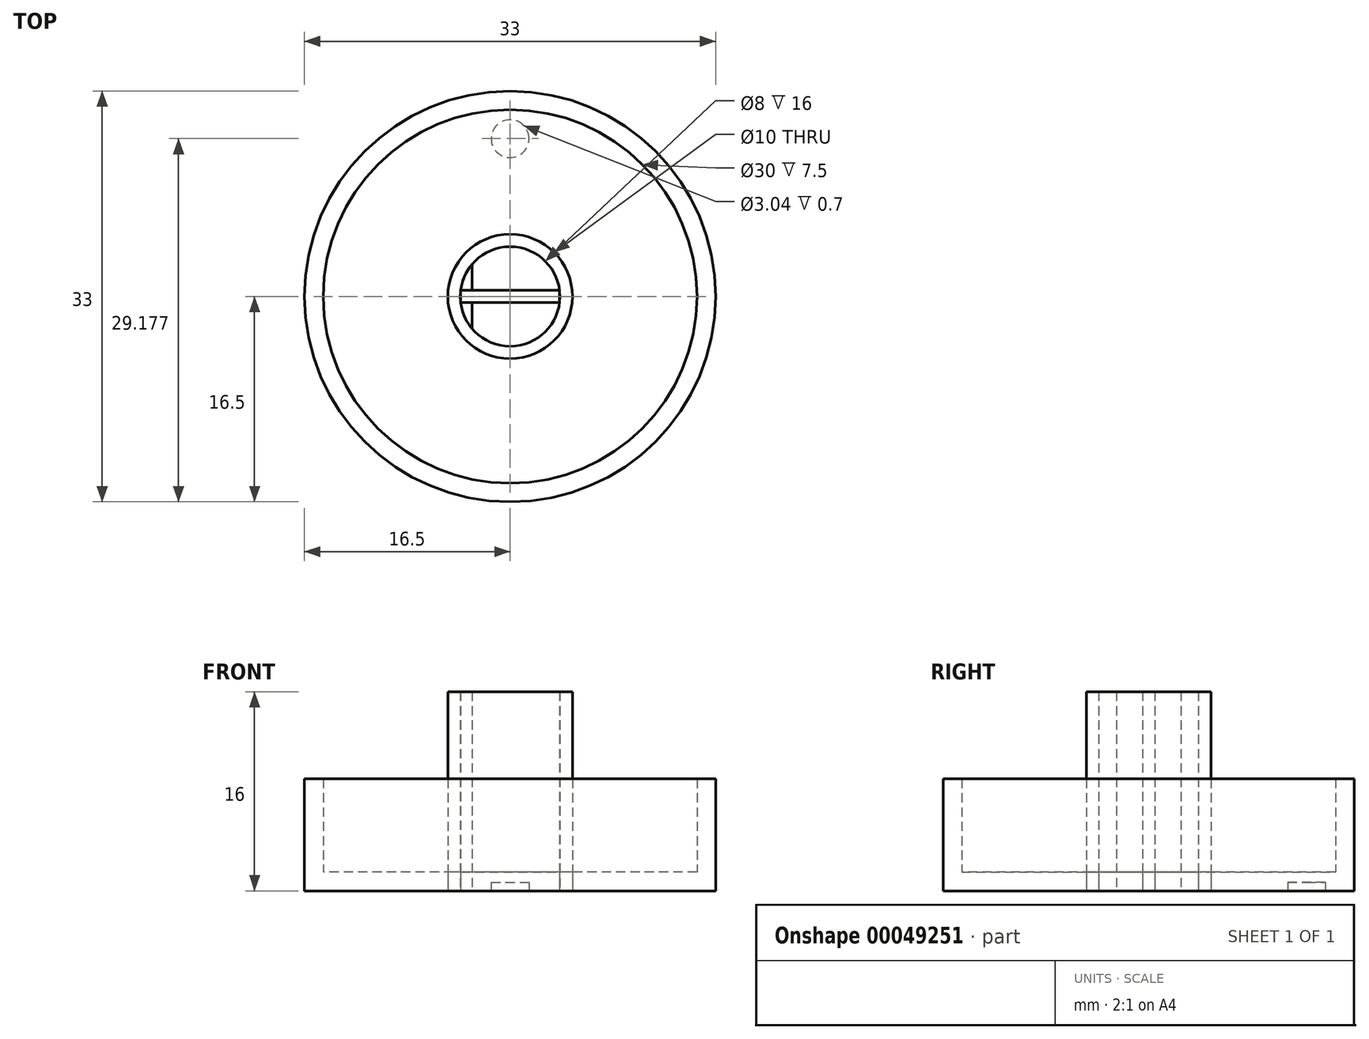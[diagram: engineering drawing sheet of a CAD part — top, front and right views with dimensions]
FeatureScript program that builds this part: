
annotation { "Feature Type Name" : "Feature", "Feature Type Description" : "" }
export const myFeature = defineFeature(function(context is Context, id is Id, definition is map)
    precondition{}
    {
        {
            var Q0;
            Q0=qCreatedBy(makeId("Top.planeOp"),FACE);
            var sketch = newSketch(context, id + "F0", { "sketchPlane" : qUnion([Q0])});
            skCircle(sketch, "E0", {"center": v(0, 0) * mm, "radius": 16.5 * mm});
            skCircle(sketch, "E1", {"center": v(0, 0) * mm, "radius": 15 * mm});
            skCircle(sketch, "E2", {"center": v(0, 0) * mm, "radius": 5 * mm});
            skCircle(sketch, "E3", {"center": v(0, 0) * mm, "radius": 4 * mm});
            skLineSegment(sketch, "E4.rect.bottom", {"start": v(-3.97, 0.5) * mm, "end": v(3.97, 0.5) * mm});
            skLineSegment(sketch, "E4.rect.top", {"start": v(-3.97, -0.5) * mm, "end": v(3.97, -0.5) * mm});
            skLineSegment(sketch, "E4.rect.left", {"start": v(-3.97, 0.5) * mm, "end": v(-3.97, -0.5) * mm});
            skLineSegment(sketch, "E4.rect.right", {"start": v(3.97, 0.5) * mm, "end": v(3.97, -0.5) * mm});
            skLineSegment(sketch, "E5", {"start": v(-3.05, 2.59) * mm, "end": v(-3.05, -2.59) * mm});
            skSolve(sketch);
        }
        {
            var Q0;
            Q0=makeQuery(id+"F0.imprint","IMPRINT",FACE,{"disambiguationData":[TD([[makeQuery(id+"F0.imprint","IMPRINT",EDGE,{"derivedFrom":sQuery(id+"F0.wireOp",EDGE,"E1")}),1.0]])]});
            var Q1;
            {var subQ0=sQuery(id+"F0.wireOp",EDGE,"E4.rect.bottom");Q1=makeQuery(id+"F0.imprint","IMPRINT",FACE,{"disambiguationData":[TD([[makeQuery(id+"F0.imprint","IMPRINT",EDGE,{"derivedFrom":subQ0}),1.0]])]});}
            var Q2;
            {var subQ0=sQuery(id+"F0.wireOp",EDGE,"E4.rect.top");Q2=makeQuery(id+"F0.imprint","IMPRINT",FACE,{"disambiguationData":[TD([[makeQuery(id+"F0.imprint","IMPRINT",EDGE,{"derivedFrom":subQ0}),-1.0]])]});}
            extrude(context, id + "F1", {"entities" : qUnion([Q0, Q1, Q2]), "depth" : 1.5 * mm});
        }
        {
            var Q0;
            Q0 = qSketchRegion(id + "F0", true);
            extrude(context, id + "F2", {"entities" : qUnion([Q0]), "operationType" : NewBodyOperationType.ADD, "depth" : 9 * mm});
        }
        {
            var Q0;
            Q0=makeQuery(id+"F0.imprint","IMPRINT",FACE,{"disambiguationData":[TD([[makeQuery(id+"F0.imprint","IMPRINT",EDGE,{"derivedFrom":sQuery(id+"F0.wireOp",EDGE,"E2")}),1.0]])]});
            var Q1;
            Q1=makeQuery(id+"F0.imprint","IMPRINT",FACE,{"disambiguationData":[TD([[makeQuery(id+"F0.imprint","IMPRINT",EDGE,{"derivedFrom":sQuery(id+"F0.wireOp",EDGE,"E4.rect.bottom")}),-1.0]])]});
            extrude(context, id + "F3", {"entities" : qUnion([Q0, Q1]), "depth" : 16 * mm});
        }
        {
            var Q0;
            {var subQ1=sQuery(id+"F0.wireOp",EDGE,"E3");var subQ3=sQuery(id+"F0.wireOp",EDGE,"E5");var subQ4=makeQuery(id+"F0.imprint","INTERSECT",VERTEX,{"disambiguationData":[OD(0.0)],"derivedFrom":[subQ1,subQ3]});Q0=makeQuery(id+"F0.imprint","IMPRINT",FACE,{"disambiguationData":[TD([[makeQuery(id+"F0.imprint","IMPRINT",EDGE,{"disambiguationData":[TD([[subQ4,-1.0]])],"derivedFrom":subQ3}),-1.0]])]});}
            var Q1;
            {var subQ1=sQuery(id+"F0.wireOp",EDGE,"E3");var subQ3=sQuery(id+"F0.wireOp",EDGE,"E5");var subQ4=makeQuery(id+"F0.imprint","INTERSECT",VERTEX,{"disambiguationData":[OD(1.0)],"derivedFrom":[subQ1,subQ3]});Q1=makeQuery(id+"F0.imprint","IMPRINT",FACE,{"disambiguationData":[TD([[makeQuery(id+"F0.imprint","IMPRINT",EDGE,{"disambiguationData":[TD([[subQ4,1.0]])],"derivedFrom":subQ3}),-1.0]])]});}
            extrude(context, id + "F4", {"entities" : qUnion([Q0, Q1]), "depth" : 16 * mm});
        }
        {
            var Q0;
            {var subQ0=sQuery(id+"F0.wireOp",EDGE,"E1");Q0=makeQuery(id+"F2.boolean.opBoolean","MERGE",FACE,{"derivedFrom":[makeQuery(id+"F1.opExtrude","CAP_FACE",FACE,{"disambiguationData":[OSD([subQ0,sQuery(id+"F0.wireOp",EDGE,"E2")])],"isStart":true}),makeQuery(id+"F2.opExtrude","CAP_FACE",FACE,{"disambiguationData":[OSD([sQuery(id+"F0.wireOp",EDGE,"E0"),subQ0])],"isStart":true})]});}
            var sketch = newSketch(context, id + "F5", { "sketchPlane" : qUnion([Q0])});
            skCircle(sketch, "E6", {"center": v(0, -12.68) * mm, "radius": 1.52 * mm});
            skSolve(sketch);
        }
        {
            var Q0;
            Q0=makeQuery(id+"F5.imprint","IMPRINT",FACE,{"disambiguationData":[TD([[makeQuery(id+"F5.imprint","IMPRINT",EDGE,{"derivedFrom":sQuery(id+"F5.wireOp",EDGE,"E6")}),1.0]])]});
            extrude(context, id + "F6", {"entities" : qUnion([Q0]), "operationType" : NewBodyOperationType.REMOVE, "oppositeDirection" : true, "depth" : 0.7 * mm});
        }
    });
